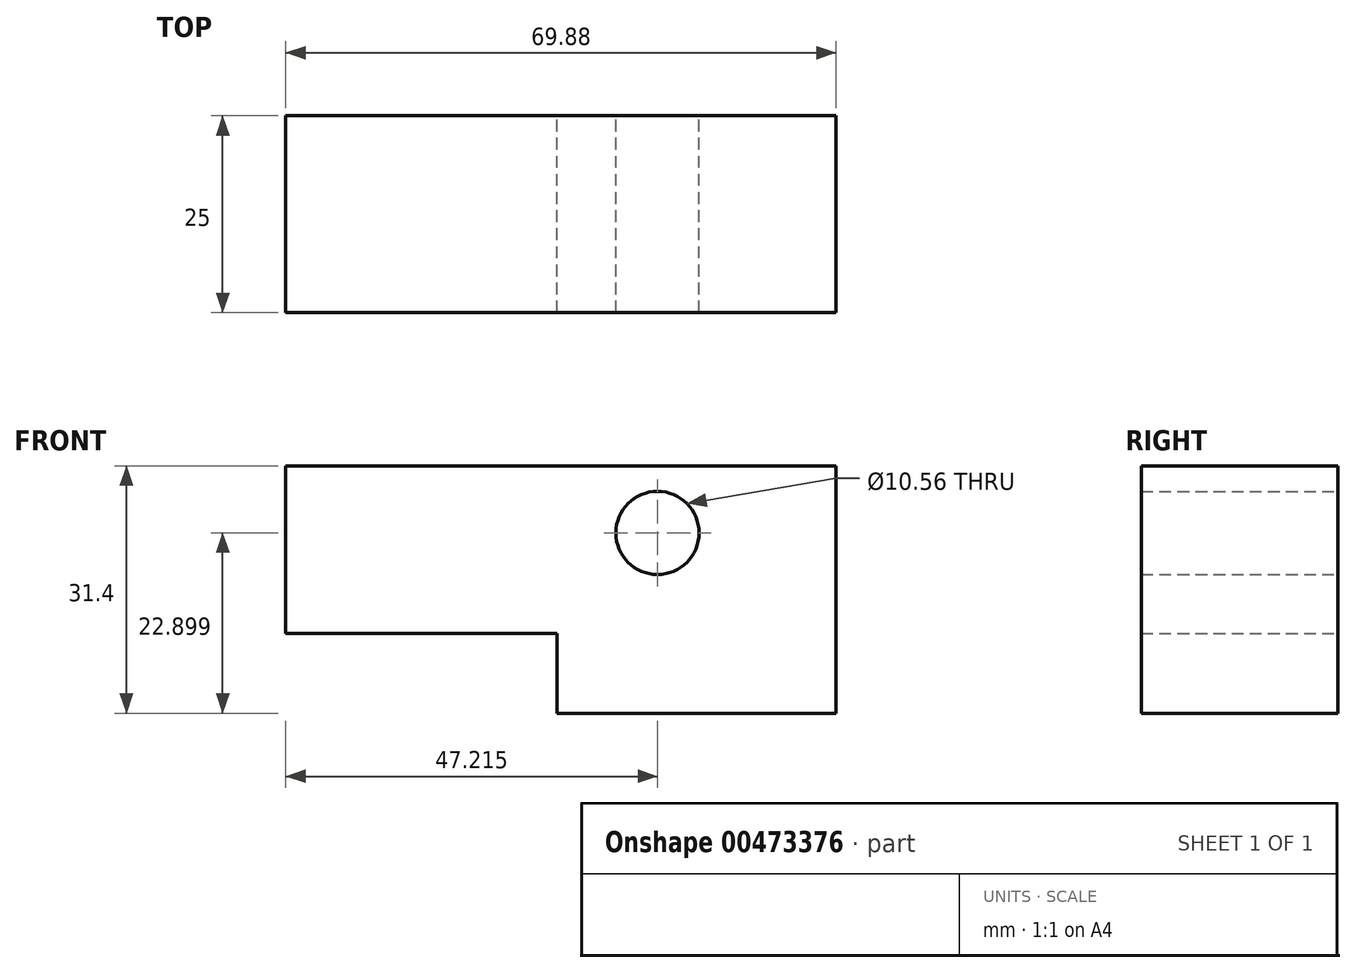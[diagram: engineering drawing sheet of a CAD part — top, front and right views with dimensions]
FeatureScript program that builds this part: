
annotation { "Feature Type Name" : "Feature", "Feature Type Description" : "" }
export const myFeature = defineFeature(function(context is Context, id is Id, definition is map)
    precondition{}
    {
        {
            var Q0;
            Q0=qCreatedBy(makeId("Front.planeOp"),FACE);
            var sketch = newSketch(context, id + "F0", { "sketchPlane" : qUnion([Q0])});
            skLineSegment(sketch, "E0.bottom", {"start": v(34.47, 0) * mm, "end": v(69.88, 0) * mm});
            skLineSegment(sketch, "E0.top", {"start": v(0, 31.4) * mm, "end": v(69.88, 31.4) * mm});
            skLineSegment(sketch, "E0.left", {"start": v(0, 10.15) * mm, "end": v(0, 31.4) * mm});
            skLineSegment(sketch, "E0.right", {"start": v(69.88, 0) * mm, "end": v(69.88, 31.4) * mm});
            skCircle(sketch, "E1", {"center": v(47.21, 22.9) * mm, "radius": 5.28 * mm});
            skLineSegment(sketch, "E2", {"start": v(0, 10.15) * mm, "end": v(34.47, 10.15) * mm});
            skLineSegment(sketch, "E3", {"start": v(34.47, 10.15) * mm, "end": v(34.47, -18.65) * mm});
            skSolve(sketch);
        }
        {
            var Q0;
            Q0 = qSketchRegion(id + "F0", true);
            extrude(context, id + "F1", {"entities" : qUnion([Q0]), "depth" : 25 * mm});
        }
    });
